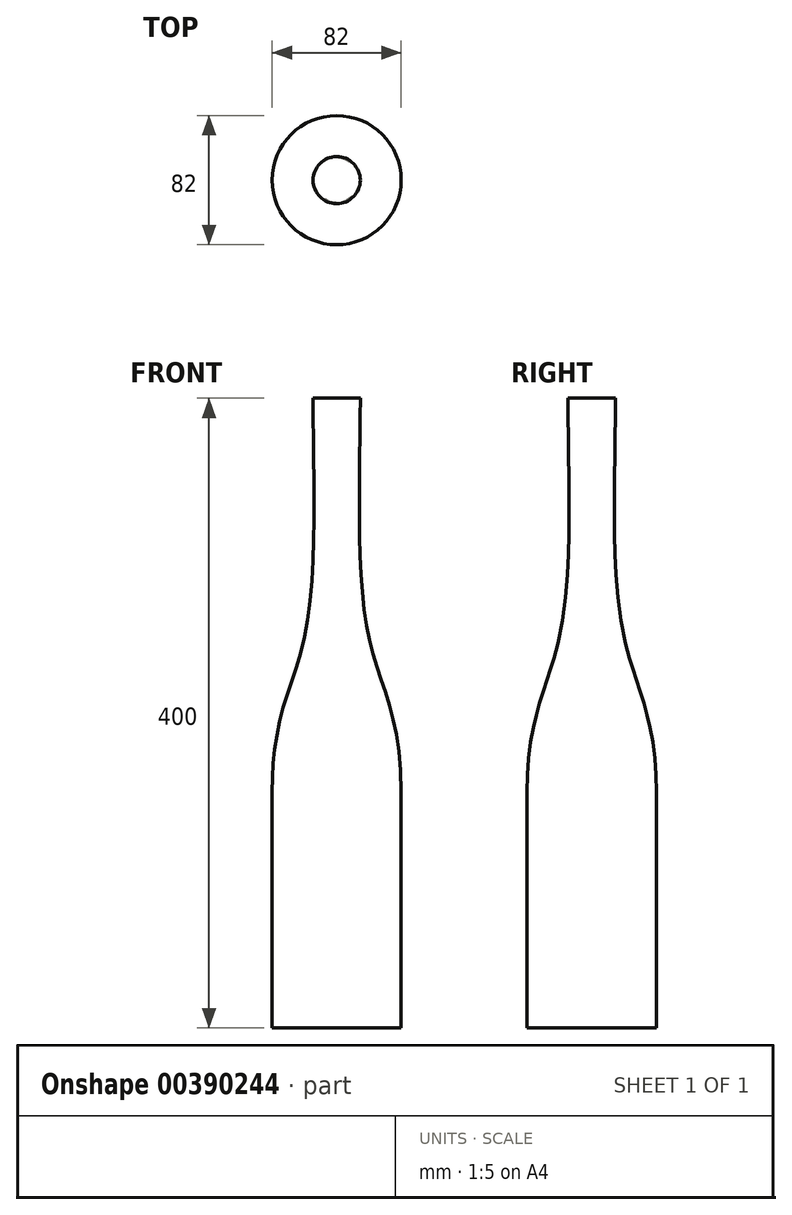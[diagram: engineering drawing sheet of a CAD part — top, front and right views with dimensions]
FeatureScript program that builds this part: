
annotation { "Feature Type Name" : "Feature", "Feature Type Description" : "" }
export const myFeature = defineFeature(function(context is Context, id is Id, definition is map)
    precondition{}
    {
        {
            var Q0;
            Q0=qCreatedBy(makeId("Front.planeOp"),FACE);
            var sketch = newSketch(context, id + "F0", { "sketchPlane" : qUnion([Q0])});
            skLineSegment(sketch, "E0.left", {"start": v(41, 0) * mm, "end": v(41, 150) * mm});
            skPoint(sketch, "E0.middle", {"position": v(0, 0) * mm});
            skLineSegment(sketch, "E1", {"start": v(0, 400) * mm, "end": v(15, 400) * mm});
            skFitSpline(sketch, "E2", {"points": [v(15, 400) * mm, v(20, 250) * mm, v(41, 150) * mm], "startDerivative": vector(0, -273.77) * mm, "endDerivative": vector(0, -331.8) * mm});
            skLineSegment(sketch, "E3", {"start": v(0, 306.73) * mm, "end": v(0, -233.73) * mm, "construction": true});
            skLineSegment(sketch, "E4", {"start": v(41, 0) * mm, "end": v(0, 0) * mm});
            skLineSegment(sketch, "E5", {"start": v(0, 400) * mm, "end": v(0, 0) * mm});
            skSolve(sketch);
        }
        {
            var Q0;
            Q0 = qSketchRegion(id + "F0", true);
            var Q1;
            Q1=sQuery(id+"F0.wireOp",EDGE,"E3");
            revolve(context, id + "F1", {"entities" : qUnion([Q0]), "axis" : qUnion([Q1]), "revolveType" : RevolveType.FULL});
        }
    });
